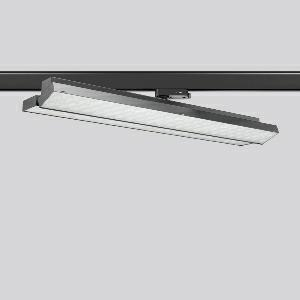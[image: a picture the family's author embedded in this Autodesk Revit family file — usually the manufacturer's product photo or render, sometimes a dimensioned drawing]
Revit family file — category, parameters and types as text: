
# Revit family: tx-move_742161_003_76_fc4b
name_source: partatom
category: Lighting Fixtures
units: mm (PartAtom-declared; Revit-internal decimal feet)

## family parameters
Cut with Voids When Loaded = No
Host = Face
Light Source = No
Part Type = Normal
Room Calculation Point = No
Round Connector Dimension = Use Diameter
Shared = No

## types (1)
- MultiLumen 1 (1 x LED Modul 830, 2900 lm, 3000)
    Apparent Load = 41 VA
    CIE Flux Codes = 90 97 99 100 100
    Color Rendering = 80
    Color Temperature = 3000
    Default Elevation = 1800 mm
    Description = Series: TX-MOVE
Multifunctional surface-mounted spotlight for area lighting. Very flat design. Housing: sheet steel, powder-coated. Rotation range: 356°. Swivel range: 90°. Consistent alignment possible with visible tilt scale. High-efficiency LED units with optimum light control thanks to clear plastic (PC) lens optics. Spezielle Mikrostrukturen reduzieren Gelbsaum. Symmetrical light distribution. With adapter for RZB 3-circuit DALI tracks. Suitable for Track on ceiling. MultiLumen: Luminous flux adjustable in 3 steps. Factory setting is the highest luminous flux. Environmentally friendly and resource-saving due to replaceable and recyclable components. Very good glare control, ideal for till areas. 
Colour: deep black, matt (RAL 9005)
Length: 570 mm
Width: 119 mm
Height: 88 mm
Lamp: LED
Socket: without socket
Colour temperature: 3000K
Colour rendering index (CRI): 80
System power: 41 W
Rated luminous flux: 5800 lm
Luminous efficiency: 141 lm/W
System power 2: 57 W
Rated luminous flux 2: 7850 lm
Luminous efficiency 2: 138 lm/W
System power 3: 73 W
Rated luminous flux 3: 9600 lm
Luminous efficiency 3: 132 lm/W
Control gear: Dimmable EVG, DALI
Protection class: I
Type of protection: IP 20
    Height = 75 mm
    Lamp = 1 x LED Modul 830
    Lamp Light Flux = 2900 lm
    Lamp count = 1
    Length = 569 mm
    Lifetime = 50000 h
    Luminous efficacy = 141 lm/W
    Manufacturer = RZB
    ModVariant = No
    Model = 742161.003.76
    Mounting Place = Ceiling
    Mounting Type = Surface mounted
    Number of Poles = 1
    OnlyDefault = Yes
    Power Factor = 1
    Product Name = TX-MOVE
    Product group = Track mounted projectors
    ProductGroupID = 301
    Protection Class = Protection class I
    Protection Degree = IP 20
    RLX_Detail_Level = 1
    RLX_Emergency_Light_Flux = 0 lm
    RLX_Emergency_Type = 0
    RLX_Emergency_Type_DB = No
    RlxData = <blob elided: 36745 chars, md5=a4a3f30a>
    Socket = socket
    Standby Power = 0 W
    System Light Flux = 5800 lm
    System Power = 41 W
    Type Comments = MultiLumen 1
    Type Image = 742162.003.jpg
    URL = http://relux.com
    VarID = multilumen_1
    Voltage = 0 V
    Weight = 0.00 kg
    Width = 119 mm

## geometry (parser evidence)
native form markers: Blend x4, Sweep x15
no freeform markers — native parametric forms only
